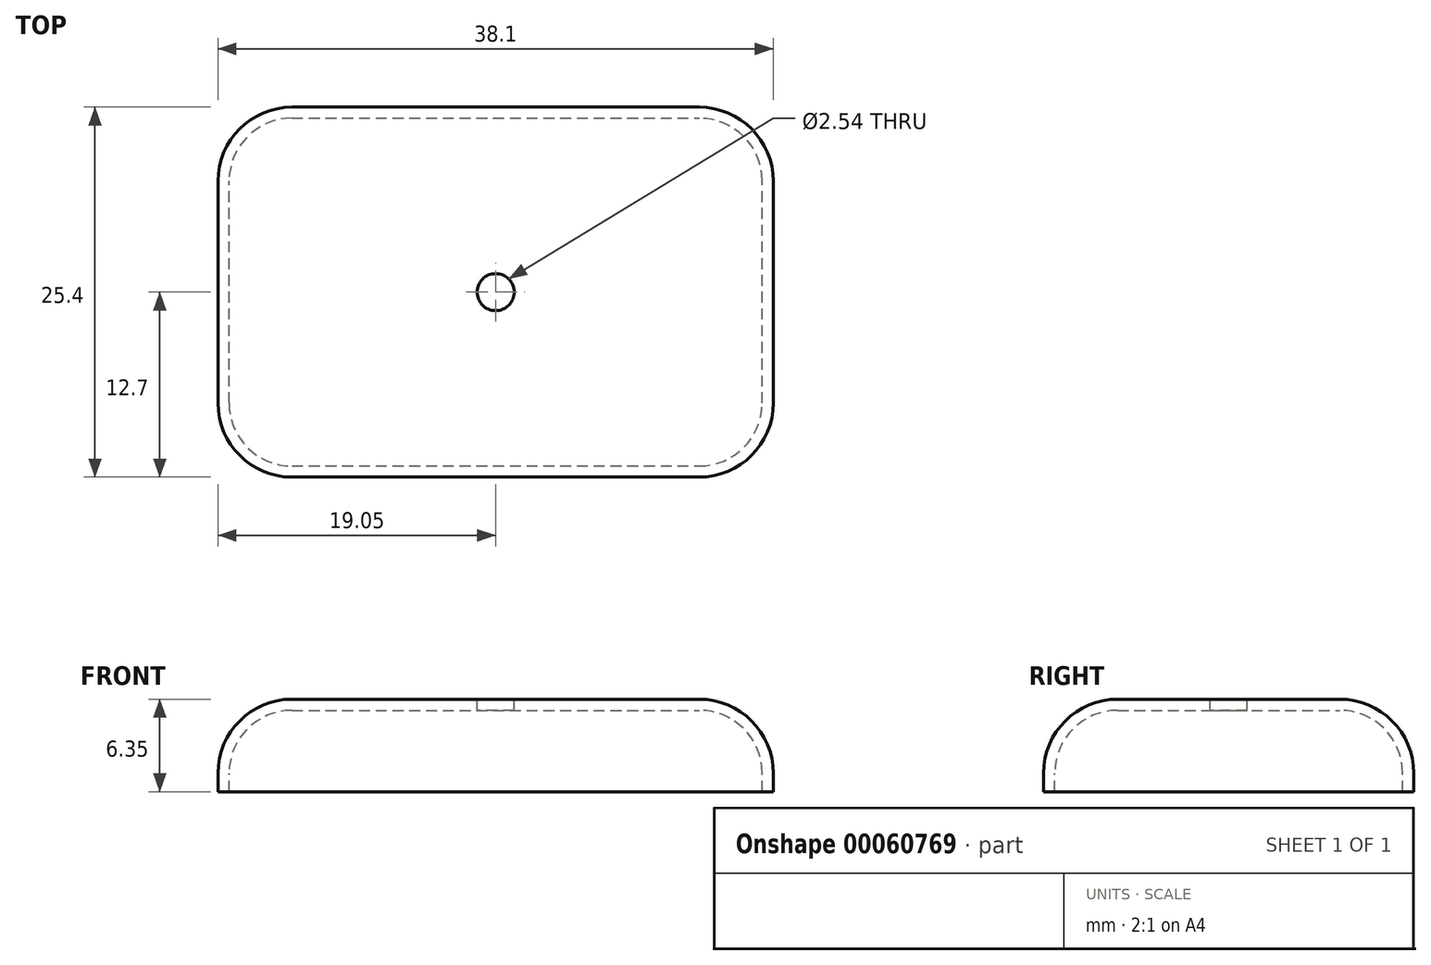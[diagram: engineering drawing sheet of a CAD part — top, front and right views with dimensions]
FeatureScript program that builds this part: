
annotation { "Feature Type Name" : "Feature", "Feature Type Description" : "" }
export const myFeature = defineFeature(function(context is Context, id is Id, definition is map)
    precondition{}
    {
        {
            var Q0;
            Q0=qCreatedBy(makeId("Top.planeOp"),FACE);
            var sketch = newSketch(context, id + "F0", { "sketchPlane" : qUnion([Q0])});
            skLineSegment(sketch, "E0.bottom", {"start": v(0, 0) * mm, "end": v(38.1, 0) * mm});
            skLineSegment(sketch, "E0.top", {"start": v(0, 25.4) * mm, "end": v(38.1, 25.4) * mm});
            skLineSegment(sketch, "E0.left", {"start": v(0, 0) * mm, "end": v(0, 25.4) * mm});
            skLineSegment(sketch, "E0.right", {"start": v(38.1, 0) * mm, "end": v(38.1, 25.4) * mm});
            skSolve(sketch);
        }
        {
            var Q0;
            Q0=makeQuery(id+"F0.imprint","IMPRINT",FACE,{"disambiguationData":[TD([[makeQuery(id+"F0.imprint","IMPRINT",EDGE,{"derivedFrom":sQuery(id+"F0.wireOp",EDGE,"E0.bottom")}),1.0]])]});
            extrude(context, id + "F1", {"entities" : qUnion([Q0]), "depth" : 6.35 * mm});
        }
        {
            var Q0;
            Q0=makeQuery(id+"F1.opExtrude","CAP_FACE",FACE,{"disambiguationData":[OSD([sQuery(id+"F0.wireOp",EDGE,"E0.bottom"),sQuery(id+"F0.wireOp",EDGE,"E0.top"),sQuery(id+"F0.wireOp",EDGE,"E0.left"),sQuery(id+"F0.wireOp",EDGE,"E0.right")])],"isStart":false});
            var Q1;
            Q1=makeQuery(id+"F1.opExtrude","SWEPT_EDGE",EDGE,{"disambiguationData":[OSD([sQuery(id+"F0.wireOp",EDGE,"E0.bottom"),sQuery(id+"F0.wireOp",EDGE,"E0.left")])]});
            var Q2;
            Q2=makeQuery(id+"F1.opExtrude","SWEPT_EDGE",EDGE,{"disambiguationData":[OSD([sQuery(id+"F0.wireOp",EDGE,"E0.bottom"),sQuery(id+"F0.wireOp",EDGE,"E0.right")])]});
            var Q3;
            Q3=makeQuery(id+"F1.opExtrude","SWEPT_EDGE",EDGE,{"disambiguationData":[OSD([sQuery(id+"F0.wireOp",EDGE,"E0.top"),sQuery(id+"F0.wireOp",EDGE,"E0.right")])]});
            var Q4;
            Q4=makeQuery(id+"F1.opExtrude","SWEPT_EDGE",EDGE,{"disambiguationData":[OSD([sQuery(id+"F0.wireOp",EDGE,"E0.top"),sQuery(id+"F0.wireOp",EDGE,"E0.left")])]});
            fillet(context, id + "F2", {"entities" : qUnion([Q0, Q1, Q2, Q3, Q4]), "radius" : 5.08 * mm, "tangentPropagation" : true, "defaultsChanged" : true, "vertexSettings" : [], "allowEdgeOverflow" : false});
        }
        {
            var Q0;
            Q0=makeQuery(id+"F1.opExtrude","CAP_FACE",FACE,{"disambiguationData":[OSD([sQuery(id+"F0.wireOp",EDGE,"E0.bottom"),sQuery(id+"F0.wireOp",EDGE,"E0.top"),sQuery(id+"F0.wireOp",EDGE,"E0.left"),sQuery(id+"F0.wireOp",EDGE,"E0.right")])],"isStart":true});
            shell(context, id + "F3", {"entities" : qUnion([Q0]), "thickness" : 0.76 * mm});
        }
        {
            var Q0;
            Q0=makeQuery(id+"F1.opExtrude","CAP_FACE",FACE,{"disambiguationData":[OSD([sQuery(id+"F0.wireOp",EDGE,"E0.bottom"),sQuery(id+"F0.wireOp",EDGE,"E0.top"),sQuery(id+"F0.wireOp",EDGE,"E0.left"),sQuery(id+"F0.wireOp",EDGE,"E0.right")])],"isStart":false});
            var sketch = newSketch(context, id + "F4", { "sketchPlane" : qUnion([Q0])});
            skCircle(sketch, "E1", {"center": v(19.05, 12.7) * mm, "radius": 1.27 * mm});
            skSolve(sketch);
        }
        {
            var Q0;
            Q0 = qSketchRegion(id + "F4", true);
            extrude(context, id + "F5", {"entities" : qUnion([Q0]), "operationType" : NewBodyOperationType.REMOVE, "flatOperationType" : FlatOperationType.REMOVE, "endBound" : BoundingType.THROUGH_ALL, "oppositeDirection" : true, "offsetDistance" : 25.4 * mm, "depth" : 25.4 * mm, "domain" : OperationDomain.MODEL});
        }
    });
